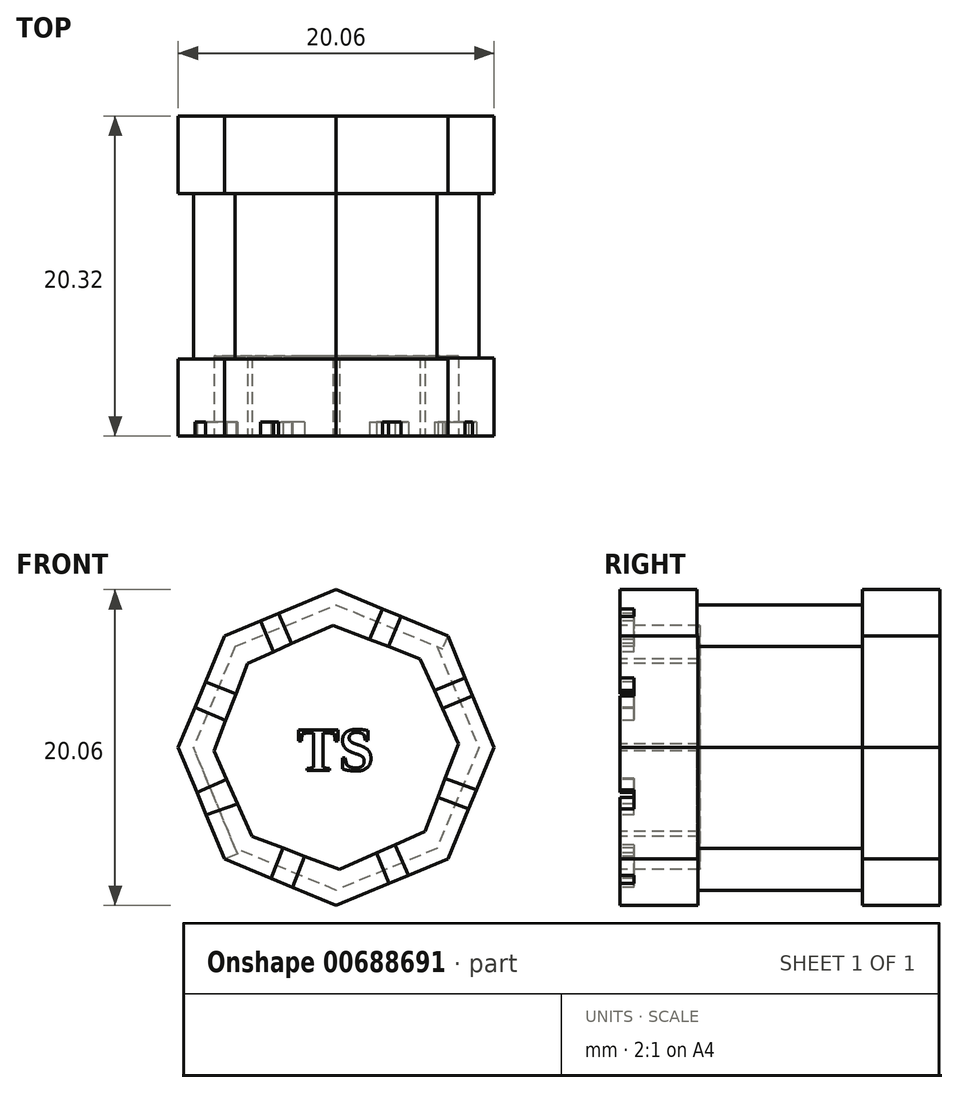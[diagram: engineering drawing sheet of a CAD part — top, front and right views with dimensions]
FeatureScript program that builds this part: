
annotation { "Feature Type Name" : "Feature", "Feature Type Description" : "" }
export const myFeature = defineFeature(function(context is Context, id is Id, definition is map)
    precondition{}
    {
        {
            var Q0;
            Q0=qCreatedBy(makeId("Front.planeOp"),FACE);
            var sketch = newSketch(context, id + "F0", { "sketchPlane" : qUnion([Q0])});
            skCircle(sketch, "E0.cCircle", {"center": v(0, 0) * mm, "radius": 10.03 * mm, "construction": true});
            skLineSegment(sketch, "E0.0", {"start": v(10.03, 0) * mm, "end": v(7.09, -7.09) * mm});
            skLineSegment(sketch, "E0.1", {"start": v(7.09, -7.09) * mm, "end": v(0, -10.03) * mm});
            skLineSegment(sketch, "E0.2", {"start": v(0, -10.03) * mm, "end": v(-7.09, -7.09) * mm});
            skLineSegment(sketch, "E0.3", {"start": v(-7.09, -7.09) * mm, "end": v(-10.03, 0) * mm});
            skLineSegment(sketch, "E0.4", {"start": v(-10.03, 0) * mm, "end": v(-7.09, 7.09) * mm});
            skLineSegment(sketch, "E0.5", {"start": v(-7.09, 7.09) * mm, "end": v(0, 10.03) * mm});
            skLineSegment(sketch, "E0.6", {"start": v(0, 10.03) * mm, "end": v(7.09, 7.09) * mm});
            skLineSegment(sketch, "E0.7", {"start": v(7.09, 7.09) * mm, "end": v(10.03, 0) * mm});
            skSolve(sketch);
        }
        {
            var Q0;
            Q0 = qSketchRegion(id + "F0", true);
            extrude(context, id + "F1", {"entities" : qUnion([Q0]), "depth" : 20.32 * mm, "offsetDistance" : 25.4 * mm});
        }
        {
            var Q0;
            Q0=makeQuery(id+"F1.opExtrude","CAP_FACE",FACE,{"disambiguationData":[OSD([sQuery(id+"F0.wireOp",EDGE,"E0.0"),sQuery(id+"F0.wireOp",EDGE,"E0.1"),sQuery(id+"F0.wireOp",EDGE,"E0.2"),sQuery(id+"F0.wireOp",EDGE,"E0.3"),sQuery(id+"F0.wireOp",EDGE,"E0.4"),sQuery(id+"F0.wireOp",EDGE,"E0.5"),sQuery(id+"F0.wireOp",EDGE,"E0.6"),sQuery(id+"F0.wireOp",EDGE,"E0.7")])],"isStart":false});
            var sketch = newSketch(context, id + "F2", { "sketchPlane" : qUnion([Q0])});
            skCircle(sketch, "E1.cCircle", {"center": v(0, 0) * mm, "radius": 7.76 * mm, "construction": true});
            skLineSegment(sketch, "E1.0", {"start": v(5.33, 5.64) * mm, "end": v(7.76, 0.21) * mm});
            skLineSegment(sketch, "E1.1", {"start": v(7.76, 0.21) * mm, "end": v(5.64, -5.33) * mm});
            skLineSegment(sketch, "E1.2", {"start": v(5.64, -5.33) * mm, "end": v(0.21, -7.76) * mm});
            skLineSegment(sketch, "E1.3", {"start": v(0.21, -7.76) * mm, "end": v(-5.33, -5.64) * mm});
            skLineSegment(sketch, "E1.4", {"start": v(-5.33, -5.64) * mm, "end": v(-7.76, -0.21) * mm});
            skLineSegment(sketch, "E1.5", {"start": v(-7.76, -0.21) * mm, "end": v(-5.64, 5.33) * mm});
            skLineSegment(sketch, "E1.6", {"start": v(-5.64, 5.33) * mm, "end": v(-0.21, 7.76) * mm});
            skLineSegment(sketch, "E1.7", {"start": v(-0.21, 7.76) * mm, "end": v(5.33, 5.64) * mm});
            skSolve(sketch);
        }
        {
            var Q0;
            Q0 = qSketchRegion(id + "F2", true);
            extrude(context, id + "F3", {"entities" : qUnion([Q0]), "operationType" : NewBodyOperationType.REMOVE, "oppositeDirection" : true, "depth" : 5.08 * mm, "offsetDistance" : 25.4 * mm});
        }
        {
            var Q0;
            Q0=makeQuery(id+"F1.opExtrude","SWEPT_FACE",FACE,{"disambiguationData":[OSD([sQuery(id+"F0.wireOp",EDGE,"E0.4")])]});
            var sketch = newSketch(context, id + "F4", { "sketchPlane" : qUnion([Q0])});
            skLineSegment(sketch, "E2.bottom", {"start": v(4.92, 3.84) * mm, "end": v(15.43, 3.84) * mm});
            skLineSegment(sketch, "E2.top", {"start": v(4.92, -3.84) * mm, "end": v(15.43, -3.84) * mm});
            skLineSegment(sketch, "E2.left", {"start": v(4.92, 3.84) * mm, "end": v(4.92, -3.84) * mm});
            skLineSegment(sketch, "E2.right", {"start": v(15.43, 3.84) * mm, "end": v(15.43, -3.84) * mm});
            skSolve(sketch);
        }
        {
            var Q0;
            Q0 = qSketchRegion(id + "F4", true);
            extrude(context, id + "F5", {"entities" : qUnion([Q0]), "operationType" : NewBodyOperationType.REMOVE, "oppositeDirection" : true, "depth" : 0.89 * mm, "offsetDistance" : 25.4 * mm});
        }
        {
            var Q0;
            Q0=makeQuery(id+"F1.opExtrude","SWEPT_FACE",FACE,{"disambiguationData":[OSD([sQuery(id+"F0.wireOp",EDGE,"E0.5")])]});
            var sketch = newSketch(context, id + "F6", { "sketchPlane" : qUnion([Q0])});
            skLineSegment(sketch, "E3.bottom", {"start": v(-3.84, -4.92) * mm, "end": v(3.84, -4.92) * mm});
            skLineSegment(sketch, "E3.top", {"start": v(-3.84, -15.43) * mm, "end": v(3.84, -15.43) * mm});
            skLineSegment(sketch, "E3.left", {"start": v(-3.84, -4.92) * mm, "end": v(-3.84, -15.43) * mm});
            skLineSegment(sketch, "E3.right", {"start": v(3.84, -4.92) * mm, "end": v(3.84, -15.43) * mm});
            skSolve(sketch);
        }
        {
            var Q0;
            Q0 = qSketchRegion(id + "F6", true);
            extrude(context, id + "F7", {"entities" : qUnion([Q0]), "operationType" : NewBodyOperationType.REMOVE, "oppositeDirection" : true, "depth" : 0.89 * mm, "offsetDistance" : 25.4 * mm});
        }
        {
            var Q0;
            Q0=makeQuery(id+"F1.opExtrude","SWEPT_FACE",FACE,{"disambiguationData":[OSD([sQuery(id+"F0.wireOp",EDGE,"E0.6")])]});
            var sketch = newSketch(context, id + "F8", { "sketchPlane" : qUnion([Q0])});
            skLineSegment(sketch, "E4.bottom", {"start": v(-3.84, -4.92) * mm, "end": v(3.84, -4.92) * mm});
            skLineSegment(sketch, "E4.top", {"start": v(-3.84, -15.43) * mm, "end": v(3.84, -15.43) * mm});
            skLineSegment(sketch, "E4.left", {"start": v(-3.84, -4.92) * mm, "end": v(-3.84, -15.43) * mm});
            skLineSegment(sketch, "E4.right", {"start": v(3.84, -4.92) * mm, "end": v(3.84, -15.43) * mm});
            skSolve(sketch);
        }
        {
            var Q0;
            Q0 = qSketchRegion(id + "F8", true);
            extrude(context, id + "F9", {"entities" : qUnion([Q0]), "operationType" : NewBodyOperationType.REMOVE, "oppositeDirection" : true, "depth" : 0.89 * mm, "offsetDistance" : 25.4 * mm});
        }
        {
            var Q0;
            Q0=makeQuery(id+"F1.opExtrude","SWEPT_FACE",FACE,{"disambiguationData":[OSD([sQuery(id+"F0.wireOp",EDGE,"E0.7")])]});
            var sketch = newSketch(context, id + "F10", { "sketchPlane" : qUnion([Q0])});
            skLineSegment(sketch, "E5.bottom", {"start": v(-4.92, 3.84) * mm, "end": v(-15.36, 3.84) * mm});
            skLineSegment(sketch, "E5.top", {"start": v(-4.92, -3.84) * mm, "end": v(-15.36, -3.84) * mm});
            skLineSegment(sketch, "E5.left", {"start": v(-4.92, 3.84) * mm, "end": v(-4.92, -3.84) * mm});
            skLineSegment(sketch, "E5.right", {"start": v(-15.36, 3.84) * mm, "end": v(-15.36, -3.84) * mm});
            skSolve(sketch);
        }
        {
            var Q0;
            Q0 = qSketchRegion(id + "F10", true);
            extrude(context, id + "F11", {"entities" : qUnion([Q0]), "operationType" : NewBodyOperationType.REMOVE, "oppositeDirection" : true, "depth" : 0.89 * mm, "offsetDistance" : 25.4 * mm});
        }
        {
            var Q0;
            Q0=makeQuery(id+"F1.opExtrude","SWEPT_FACE",FACE,{"disambiguationData":[OSD([sQuery(id+"F0.wireOp",EDGE,"E0.0")])]});
            var sketch = newSketch(context, id + "F12", { "sketchPlane" : qUnion([Q0])});
            skLineSegment(sketch, "E6.bottom", {"start": v(-4.92, 3.84) * mm, "end": v(-15.36, 3.84) * mm});
            skLineSegment(sketch, "E6.top", {"start": v(-4.92, -3.84) * mm, "end": v(-15.36, -3.84) * mm});
            skLineSegment(sketch, "E6.left", {"start": v(-4.92, 3.84) * mm, "end": v(-4.92, -3.84) * mm});
            skLineSegment(sketch, "E6.right", {"start": v(-15.36, 3.84) * mm, "end": v(-15.36, -3.84) * mm});
            skSolve(sketch);
        }
        {
            var Q0;
            Q0 = qSketchRegion(id + "F12", true);
            extrude(context, id + "F13", {"entities" : qUnion([Q0]), "operationType" : NewBodyOperationType.REMOVE, "oppositeDirection" : true, "depth" : 0.89 * mm, "offsetDistance" : 25.4 * mm});
        }
        {
            var Q0;
            Q0=makeQuery(id+"F1.opExtrude","SWEPT_FACE",FACE,{"disambiguationData":[OSD([sQuery(id+"F0.wireOp",EDGE,"E0.1")])]});
            var sketch = newSketch(context, id + "F14", { "sketchPlane" : qUnion([Q0])});
            skLineSegment(sketch, "E7.bottom", {"start": v(3.84, 4.92) * mm, "end": v(-3.84, 4.92) * mm});
            skLineSegment(sketch, "E7.top", {"start": v(3.84, 15.36) * mm, "end": v(-3.84, 15.36) * mm});
            skLineSegment(sketch, "E7.left", {"start": v(3.84, 4.92) * mm, "end": v(3.84, 15.36) * mm});
            skLineSegment(sketch, "E7.right", {"start": v(-3.84, 4.92) * mm, "end": v(-3.84, 15.36) * mm});
            skSolve(sketch);
        }
        {
            var Q0;
            Q0 = qSketchRegion(id + "F14", true);
            extrude(context, id + "F15", {"entities" : qUnion([Q0]), "operationType" : NewBodyOperationType.REMOVE, "oppositeDirection" : true, "depth" : 0.89 * mm, "offsetDistance" : 25.4 * mm});
        }
        {
            var Q0;
            Q0=makeQuery(id+"F1.opExtrude","SWEPT_FACE",FACE,{"disambiguationData":[OSD([sQuery(id+"F0.wireOp",EDGE,"E0.2")])]});
            var sketch = newSketch(context, id + "F16", { "sketchPlane" : qUnion([Q0])});
            skLineSegment(sketch, "E8.bottom", {"start": v(3.84, 4.92) * mm, "end": v(-3.84, 4.92) * mm});
            skLineSegment(sketch, "E8.top", {"start": v(3.84, 15.36) * mm, "end": v(-3.84, 15.36) * mm});
            skLineSegment(sketch, "E8.left", {"start": v(3.84, 4.92) * mm, "end": v(3.84, 15.36) * mm});
            skLineSegment(sketch, "E8.right", {"start": v(-3.84, 4.92) * mm, "end": v(-3.84, 15.36) * mm});
            skSolve(sketch);
        }
        {
            var Q0;
            Q0 = qSketchRegion(id + "F16", true);
            extrude(context, id + "F17", {"entities" : qUnion([Q0]), "operationType" : NewBodyOperationType.REMOVE, "oppositeDirection" : true, "depth" : 0.89 * mm, "offsetDistance" : 25.4 * mm});
        }
        {
            var Q0;
            Q0=makeQuery(id+"F1.opExtrude","SWEPT_FACE",FACE,{"disambiguationData":[OSD([sQuery(id+"F0.wireOp",EDGE,"E0.3")])]});
            var sketch = newSketch(context, id + "F18", { "sketchPlane" : qUnion([Q0])});
            skLineSegment(sketch, "E9.bottom", {"start": v(4.92, -3.84) * mm, "end": v(15.43, -3.84) * mm});
            skLineSegment(sketch, "E9.top", {"start": v(4.92, 3.84) * mm, "end": v(15.43, 3.84) * mm});
            skLineSegment(sketch, "E9.left", {"start": v(4.92, -3.84) * mm, "end": v(4.92, 3.84) * mm});
            skLineSegment(sketch, "E9.right", {"start": v(15.43, -3.84) * mm, "end": v(15.43, 3.84) * mm});
            skSolve(sketch);
        }
        {
            var Q0;
            Q0 = qSketchRegion(id + "F18", true);
            extrude(context, id + "F19", {"entities" : qUnion([Q0]), "operationType" : NewBodyOperationType.REMOVE, "oppositeDirection" : true, "depth" : 0.89 * mm, "offsetDistance" : 25.4 * mm});
        }
        {
            var Q0;
            Q0=makeQuery(id+"F1.opExtrude","CAP_FACE",FACE,{"disambiguationData":[OSD([sQuery(id+"F0.wireOp",EDGE,"E0.0"),sQuery(id+"F0.wireOp",EDGE,"E0.1"),sQuery(id+"F0.wireOp",EDGE,"E0.2"),sQuery(id+"F0.wireOp",EDGE,"E0.3"),sQuery(id+"F0.wireOp",EDGE,"E0.4"),sQuery(id+"F0.wireOp",EDGE,"E0.5"),sQuery(id+"F0.wireOp",EDGE,"E0.6"),sQuery(id+"F0.wireOp",EDGE,"E0.7")])],"isStart":false});
            var sketch = newSketch(context, id + "F20", { "sketchPlane" : qUnion([Q0])});
            skLineSegment(sketch, "E10", {"start": v(2.95, 8.8) * mm, "end": v(4.12, 8.32) * mm});
            skLineSegment(sketch, "E11", {"start": v(4.12, 8.32) * mm, "end": v(3.32, 6.4) * mm});
            skLineSegment(sketch, "E12", {"start": v(3.32, 6.4) * mm, "end": v(2.13, 6.86) * mm});
            skLineSegment(sketch, "E13", {"start": v(2.13, 6.86) * mm, "end": v(2.95, 8.8) * mm});
            skSolve(sketch);
        }
        {
            var Q0;
            Q0 = qSketchRegion(id + "F20", true);
            extrude(context, id + "F21", {"entities" : qUnion([Q0]), "operationType" : NewBodyOperationType.REMOVE, "oppositeDirection" : true, "depth" : 0.89 * mm, "offsetDistance" : 25.4 * mm});
        }
        {
            var Q0;
            Q0=makeQuery(id+"F1.opExtrude","CAP_FACE",FACE,{"disambiguationData":[OSD([sQuery(id+"F0.wireOp",EDGE,"E0.0"),sQuery(id+"F0.wireOp",EDGE,"E0.1"),sQuery(id+"F0.wireOp",EDGE,"E0.2"),sQuery(id+"F0.wireOp",EDGE,"E0.3"),sQuery(id+"F0.wireOp",EDGE,"E0.4"),sQuery(id+"F0.wireOp",EDGE,"E0.5"),sQuery(id+"F0.wireOp",EDGE,"E0.6"),sQuery(id+"F0.wireOp",EDGE,"E0.7")])],"isStart":false});
            var sketch = newSketch(context, id + "F22", { "sketchPlane" : qUnion([Q0])});
            skLineSegment(sketch, "E14", {"start": v(8.2, 4.42) * mm, "end": v(8.67, 3.26) * mm});
            skLineSegment(sketch, "E15", {"start": v(8.67, 3.26) * mm, "end": v(6.75, 2.46) * mm});
            skLineSegment(sketch, "E16", {"start": v(6.75, 2.46) * mm, "end": v(6.23, 3.63) * mm});
            skLineSegment(sketch, "E17", {"start": v(6.23, 3.63) * mm, "end": v(8.2, 4.42) * mm});
            skSolve(sketch);
        }
        {
            var Q0;
            Q0 = qSketchRegion(id + "F22", true);
            extrude(context, id + "F23", {"entities" : qUnion([Q0]), "operationType" : NewBodyOperationType.REMOVE, "oppositeDirection" : true, "depth" : 0.89 * mm, "offsetDistance" : 25.4 * mm});
        }
        {
            var Q0;
            {var subQ0=sQuery(id+"F0.wireOp",EDGE,"E0.7");var subQ1=sQuery(id+"F0.wireOp",EDGE,"E0.6");var subQ2=sQuery(id+"F0.wireOp",EDGE,"E0.5");var subQ3=sQuery(id+"F0.wireOp",EDGE,"E0.4");var subQ4=sQuery(id+"F0.wireOp",EDGE,"E0.0");var subQ5=sQuery(id+"F0.wireOp",EDGE,"E0.3");var subQ6=sQuery(id+"F0.wireOp",EDGE,"E0.1");var subQ7=sQuery(id+"F0.wireOp",EDGE,"E0.2");Q0=makeQuery(id+"F23.boolean.opBoolean","SPLIT",FACE,{"disambiguationData":[TD([makeQuery(id+"F1.opExtrude","SWEPT_FACE",FACE,{"disambiguationData":[OSD([subQ4])]})])],"derivedFrom":makeQuery(id+"F1.opExtrude","CAP_FACE",FACE,{"disambiguationData":[OSD([subQ4,subQ6,subQ7,subQ5,subQ3,subQ2,subQ1,subQ0])],"isStart":false})});}
            var sketch = newSketch(context, id + "F24", { "sketchPlane" : qUnion([Q0])});
            skLineSegment(sketch, "E18", {"start": v(8.9, -2.7) * mm, "end": v(8.4, -3.91) * mm});
            skLineSegment(sketch, "E19", {"start": v(8.4, -3.91) * mm, "end": v(6.46, -3.17) * mm});
            skLineSegment(sketch, "E20", {"start": v(6.46, -3.17) * mm, "end": v(6.92, -1.98) * mm});
            skLineSegment(sketch, "E21", {"start": v(6.92, -1.98) * mm, "end": v(8.9, -2.7) * mm});
            skSolve(sketch);
        }
        {
            var Q0;
            Q0 = qSketchRegion(id + "F24", true);
            extrude(context, id + "F25", {"entities" : qUnion([Q0]), "operationType" : NewBodyOperationType.REMOVE, "oppositeDirection" : true, "depth" : 0.89 * mm, "offsetDistance" : 25.4 * mm});
        }
        {
            var Q0;
            {var subQ3=sQuery(id+"F0.wireOp",EDGE,"E0.6");var subQ6=sQuery(id+"F0.wireOp",EDGE,"E0.5");var subQ8=sQuery(id+"F0.wireOp",EDGE,"E0.4");var subQ10=sQuery(id+"F0.wireOp",EDGE,"E0.0");var subQ11=makeQuery(id+"F1.opExtrude","SWEPT_FACE",FACE,{"disambiguationData":[OSD([subQ10])]});var subQ12=sQuery(id+"F0.wireOp",EDGE,"E0.3");var subQ14=sQuery(id+"F0.wireOp",EDGE,"E0.1");var subQ15=makeQuery(id+"F1.opExtrude","SWEPT_FACE",FACE,{"disambiguationData":[OSD([subQ14])]});var subQ16=sQuery(id+"F0.wireOp",EDGE,"E0.2");var subQ22=sQuery(id+"F0.wireOp",EDGE,"E0.7");Q0=makeQuery(id+"F25.boolean.opBoolean","SPLIT",FACE,{"disambiguationData":[TD([subQ15])],"derivedFrom":makeQuery(id+"F23.boolean.opBoolean","SPLIT",FACE,{"disambiguationData":[TD([subQ11])],"derivedFrom":makeQuery(id+"F1.opExtrude","CAP_FACE",FACE,{"disambiguationData":[OSD([subQ10,subQ14,subQ16,subQ12,subQ8,subQ6,subQ3,subQ22])],"isStart":false})})});}
            var sketch = newSketch(context, id + "F26", { "sketchPlane" : qUnion([Q0])});
            skLineSegment(sketch, "E22", {"start": v(-4.8, 8.04) * mm, "end": v(-3.67, 8.5) * mm});
            skLineSegment(sketch, "E23", {"start": v(-3.67, 8.5) * mm, "end": v(-2.82, 6.6) * mm});
            skLineSegment(sketch, "E24", {"start": v(-2.82, 6.6) * mm, "end": v(-3.97, 6.08) * mm});
            skLineSegment(sketch, "E25", {"start": v(-3.97, 6.08) * mm, "end": v(-4.8, 8.04) * mm});
            skSolve(sketch);
        }
        {
            var Q0;
            Q0 = qSketchRegion(id + "F26", true);
            extrude(context, id + "F27", {"entities" : qUnion([Q0]), "operationType" : NewBodyOperationType.REMOVE, "oppositeDirection" : true, "depth" : 0.89 * mm, "offsetDistance" : 25.4 * mm});
        }
        {
            var Q0;
            {var subQ4=sQuery(id+"F0.wireOp",EDGE,"E0.5");var subQ6=sQuery(id+"F0.wireOp",EDGE,"E0.4");var subQ8=sQuery(id+"F0.wireOp",EDGE,"E0.0");var subQ9=makeQuery(id+"F1.opExtrude","SWEPT_FACE",FACE,{"disambiguationData":[OSD([subQ8])]});var subQ10=sQuery(id+"F0.wireOp",EDGE,"E0.3");var subQ12=sQuery(id+"F0.wireOp",EDGE,"E0.1");var subQ13=makeQuery(id+"F1.opExtrude","SWEPT_FACE",FACE,{"disambiguationData":[OSD([subQ12])]});var subQ14=sQuery(id+"F0.wireOp",EDGE,"E0.2");var subQ20=sQuery(id+"F0.wireOp",EDGE,"E0.6");var subQ23=sQuery(id+"F0.wireOp",EDGE,"E0.7");Q0=makeQuery(id+"F27.boolean.opBoolean","SPLIT",FACE,{"disambiguationData":[TD([subQ9])],"derivedFrom":makeQuery(id+"F25.boolean.opBoolean","SPLIT",FACE,{"disambiguationData":[TD([subQ13])],"derivedFrom":makeQuery(id+"F23.boolean.opBoolean","SPLIT",FACE,{"disambiguationData":[TD([subQ9])],"derivedFrom":makeQuery(id+"F1.opExtrude","CAP_FACE",FACE,{"disambiguationData":[OSD([subQ8,subQ12,subQ14,subQ10,subQ6,subQ4,subQ20,subQ23])],"isStart":false})})})});}
            var sketch = newSketch(context, id + "F28", { "sketchPlane" : qUnion([Q0])});
            skLineSegment(sketch, "E26", {"start": v(-3.36, -6.4) * mm, "end": v(-2.01, -6.9) * mm});
            skLineSegment(sketch, "E27", {"start": v(-2.01, -6.9) * mm, "end": v(-2.77, -8.88) * mm});
            skLineSegment(sketch, "E28", {"start": v(-2.77, -8.88) * mm, "end": v(-4.14, -8.3) * mm});
            skLineSegment(sketch, "E29", {"start": v(-4.14, -8.3) * mm, "end": v(-3.36, -6.4) * mm});
            skSolve(sketch);
        }
        {
            var Q0;
            Q0 = qSketchRegion(id + "F28", true);
            extrude(context, id + "F29", {"entities" : qUnion([Q0]), "operationType" : NewBodyOperationType.REMOVE, "oppositeDirection" : true, "depth" : 0.89 * mm, "offsetDistance" : 25.4 * mm});
        }
        {
            var Q0;
            {var subQ1=sQuery(id+"F0.wireOp",EDGE,"E0.2");var subQ3=sQuery(id+"F0.wireOp",EDGE,"E0.1");var subQ4=makeQuery(id+"F1.opExtrude","SWEPT_FACE",FACE,{"disambiguationData":[OSD([subQ3])]});var subQ5=sQuery(id+"F0.wireOp",EDGE,"E0.0");var subQ6=makeQuery(id+"F1.opExtrude","SWEPT_FACE",FACE,{"disambiguationData":[OSD([subQ5])]});var subQ12=sQuery(id+"F0.wireOp",EDGE,"E0.5");var subQ14=sQuery(id+"F0.wireOp",EDGE,"E0.4");var subQ16=sQuery(id+"F0.wireOp",EDGE,"E0.3");var subQ21=sQuery(id+"F0.wireOp",EDGE,"E0.6");var subQ24=sQuery(id+"F0.wireOp",EDGE,"E0.7");Q0=makeQuery(id+"F29.boolean.opBoolean","SPLIT",FACE,{"disambiguationData":[TD([subQ6])],"derivedFrom":makeQuery(id+"F27.boolean.opBoolean","SPLIT",FACE,{"disambiguationData":[TD([subQ6])],"derivedFrom":makeQuery(id+"F25.boolean.opBoolean","SPLIT",FACE,{"disambiguationData":[TD([subQ4])],"derivedFrom":makeQuery(id+"F23.boolean.opBoolean","SPLIT",FACE,{"disambiguationData":[TD([subQ6])],"derivedFrom":makeQuery(id+"F1.opExtrude","CAP_FACE",FACE,{"disambiguationData":[OSD([subQ5,subQ3,subQ1,subQ16,subQ14,subQ12,subQ21,subQ24])],"isStart":false})})})})});}
            var sketch = newSketch(context, id + "F30", { "sketchPlane" : qUnion([Q0])});
            skLineSegment(sketch, "E30", {"start": v(4.48, -8.17) * mm, "end": v(3.35, -8.64) * mm});
            skLineSegment(sketch, "E31", {"start": v(3.35, -8.64) * mm, "end": v(2.56, -6.71) * mm});
            skLineSegment(sketch, "E32", {"start": v(2.56, -6.71) * mm, "end": v(3.74, -6.18) * mm});
            skLineSegment(sketch, "E33", {"start": v(3.74, -6.18) * mm, "end": v(4.6, -8.12) * mm});
            skLineSegment(sketch, "E34", {"start": v(4.6, -8.12) * mm, "end": v(4.48, -8.17) * mm});
            skSolve(sketch);
        }
        {
            var Q0;
            Q0 = qSketchRegion(id + "F30", true);
            extrude(context, id + "F31", {"entities" : qUnion([Q0]), "operationType" : NewBodyOperationType.REMOVE, "oppositeDirection" : true, "depth" : 0.89 * mm, "offsetDistance" : 25.4 * mm});
        }
        {
            var Q0;
            {var subQ0=sQuery(id+"F0.wireOp",EDGE,"E0.5");var subQ2=sQuery(id+"F0.wireOp",EDGE,"E0.4");var subQ4=sQuery(id+"F0.wireOp",EDGE,"E0.3");var subQ5=makeQuery(id+"F1.opExtrude","SWEPT_FACE",FACE,{"disambiguationData":[OSD([subQ4])]});var subQ6=sQuery(id+"F0.wireOp",EDGE,"E0.2");var subQ15=sQuery(id+"F0.wireOp",EDGE,"E0.0");var subQ16=makeQuery(id+"F1.opExtrude","SWEPT_FACE",FACE,{"disambiguationData":[OSD([subQ15])]});var subQ17=sQuery(id+"F0.wireOp",EDGE,"E0.1");var subQ18=makeQuery(id+"F1.opExtrude","SWEPT_FACE",FACE,{"disambiguationData":[OSD([subQ17])]});var subQ21=sQuery(id+"F0.wireOp",EDGE,"E0.6");var subQ24=sQuery(id+"F0.wireOp",EDGE,"E0.7");Q0=makeQuery(id+"F29.boolean.opBoolean","SPLIT",FACE,{"disambiguationData":[TD([subQ5])],"derivedFrom":makeQuery(id+"F27.boolean.opBoolean","SPLIT",FACE,{"disambiguationData":[TD([subQ16])],"derivedFrom":makeQuery(id+"F25.boolean.opBoolean","SPLIT",FACE,{"disambiguationData":[TD([subQ18])],"derivedFrom":makeQuery(id+"F23.boolean.opBoolean","SPLIT",FACE,{"disambiguationData":[TD([subQ16])],"derivedFrom":makeQuery(id+"F1.opExtrude","CAP_FACE",FACE,{"disambiguationData":[OSD([subQ15,subQ17,subQ6,subQ4,subQ2,subQ0,subQ21,subQ24])],"isStart":false})})})})});}
            var sketch = newSketch(context, id + "F32", { "sketchPlane" : qUnion([Q0])});
            skLineSegment(sketch, "E35", {"start": v(-6.94, 1.91) * mm, "end": v(-6.37, 3.41) * mm});
            skLineSegment(sketch, "E36", {"start": v(-6.37, 3.41) * mm, "end": v(-8.3, 4.15) * mm});
            skLineSegment(sketch, "E37", {"start": v(-8.3, 4.15) * mm, "end": v(-8.97, 2.54) * mm});
            skLineSegment(sketch, "E38", {"start": v(-8.97, 2.54) * mm, "end": v(-7.01, 1.73) * mm});
            skLineSegment(sketch, "E39", {"start": v(-7.01, 1.73) * mm, "end": v(-6.94, 1.91) * mm});
            skSolve(sketch);
        }
        {
            var Q0;
            Q0 = qSketchRegion(id + "F32", true);
            extrude(context, id + "F33", {"entities" : qUnion([Q0]), "operationType" : NewBodyOperationType.REMOVE, "oppositeDirection" : true, "depth" : 0.89 * mm, "offsetDistance" : 25.4 * mm});
        }
        {
            var Q0;
            {var subQ1=sQuery(id+"F0.wireOp",EDGE,"E0.4");var subQ4=sQuery(id+"F0.wireOp",EDGE,"E0.3");var subQ5=makeQuery(id+"F1.opExtrude","SWEPT_FACE",FACE,{"disambiguationData":[OSD([subQ4])]});var subQ6=sQuery(id+"F0.wireOp",EDGE,"E0.2");var subQ7=makeQuery(id+"F1.opExtrude","SWEPT_FACE",FACE,{"disambiguationData":[OSD([subQ6])]});var subQ10=sQuery(id+"F0.wireOp",EDGE,"E0.5");var subQ16=sQuery(id+"F0.wireOp",EDGE,"E0.0");var subQ17=makeQuery(id+"F1.opExtrude","SWEPT_FACE",FACE,{"disambiguationData":[OSD([subQ16])]});var subQ18=sQuery(id+"F0.wireOp",EDGE,"E0.1");var subQ19=makeQuery(id+"F1.opExtrude","SWEPT_FACE",FACE,{"disambiguationData":[OSD([subQ18])]});var subQ22=sQuery(id+"F0.wireOp",EDGE,"E0.6");var subQ25=sQuery(id+"F0.wireOp",EDGE,"E0.7");Q0=makeQuery(id+"F33.boolean.opBoolean","SPLIT",FACE,{"disambiguationData":[TD([subQ7])],"derivedFrom":makeQuery(id+"F29.boolean.opBoolean","SPLIT",FACE,{"disambiguationData":[TD([subQ5])],"derivedFrom":makeQuery(id+"F27.boolean.opBoolean","SPLIT",FACE,{"disambiguationData":[TD([subQ17])],"derivedFrom":makeQuery(id+"F25.boolean.opBoolean","SPLIT",FACE,{"disambiguationData":[TD([subQ19])],"derivedFrom":makeQuery(id+"F23.boolean.opBoolean","SPLIT",FACE,{"disambiguationData":[TD([subQ17])],"derivedFrom":makeQuery(id+"F1.opExtrude","CAP_FACE",FACE,{"disambiguationData":[OSD([subQ16,subQ18,subQ6,subQ4,subQ1,subQ10,subQ22,subQ25])],"isStart":false})})})})})});}
            var sketch = newSketch(context, id + "F34", { "sketchPlane" : qUnion([Q0])});
            skLineSegment(sketch, "E40", {"start": v(-6.26, -3.57) * mm, "end": v(-6.95, -2.02) * mm});
            skLineSegment(sketch, "E41", {"start": v(-6.95, -2.02) * mm, "end": v(-8.84, -2.86) * mm});
            skLineSegment(sketch, "E42", {"start": v(-8.84, -2.86) * mm, "end": v(-8.26, -4.27) * mm});
            skLineSegment(sketch, "E43", {"start": v(-8.26, -4.27) * mm, "end": v(-6.26, -3.57) * mm});
            skSolve(sketch);
        }
        {
            var Q0;
            Q0 = qSketchRegion(id + "F34", true);
            extrude(context, id + "F35", {"entities" : qUnion([Q0]), "operationType" : NewBodyOperationType.REMOVE, "oppositeDirection" : true, "depth" : 0.89 * mm, "offsetDistance" : 25.4 * mm});
        }
        {
            var Q0;
            Q0=makeQuery(id+"F3.boolean.opBoolean","COPY",FACE,{"derivedFrom":makeQuery(id+"F3.opExtrude","CAP_FACE",FACE,{"disambiguationData":[OSD([sQuery(id+"F2.wireOp",EDGE,"E1.0"),sQuery(id+"F2.wireOp",EDGE,"E1.1"),sQuery(id+"F2.wireOp",EDGE,"E1.2"),sQuery(id+"F2.wireOp",EDGE,"E1.3"),sQuery(id+"F2.wireOp",EDGE,"E1.4"),sQuery(id+"F2.wireOp",EDGE,"E1.5"),sQuery(id+"F2.wireOp",EDGE,"E1.6"),sQuery(id+"F2.wireOp",EDGE,"E1.7")])],"isStart":false})});
            var sketch = newSketch(context, id + "F36", { "sketchPlane" : qUnion([Q0])});
            skText(sketch, "E44", { "text": "TS", "fontName": "Tinos-Bold.ttf"});
            const initialGuessF36  = {"E44": [-0.00245, -0.00146, 1, 0, 0.00284]};
            skSetInitialGuess(sketch, initialGuessF36);
            skSolve(sketch);
        }
        {
            var Q0;
            Q0 = qSketchRegion(id + "F36", true);
            extrude(context, id + "F37", {"entities" : qUnion([Q0]), "operationType" : NewBodyOperationType.ADD, "depth" : 0.13 * mm, "offsetDistance" : 25.4 * mm});
        }
    });
